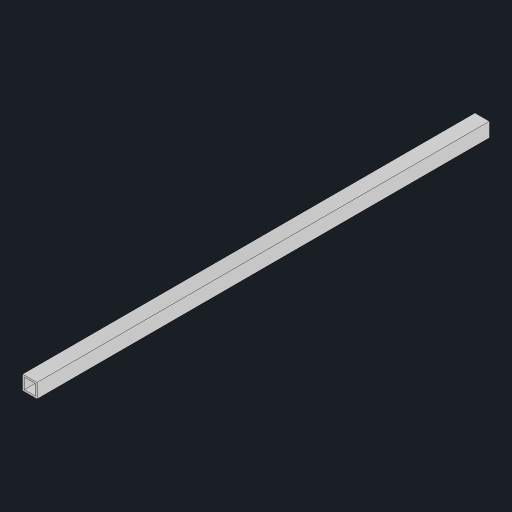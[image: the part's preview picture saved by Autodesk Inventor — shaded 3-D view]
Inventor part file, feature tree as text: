
AUTODESK INVENTOR PART (.ipt)
format: ipt  version: 2023.2 (Build 272271030, 271C)  size: 89,088 bytes
history: native  units: mm
features: extrude x1, sketch x1
ambient origin geometry x8: Origin, YZ Plane, XZ Plane, XY Plane, X Axis, Y Axis, Z Axis, Center Point
bodies: Solid1 (feature_tree)
feature tree (2):
  extrude  "Extrusion1"  Depth=0.4mm
  sketch  "Sketch1"  dims[d0=3.175mm d1=0.4mm d2=100.0mm d3=0.0mm]
